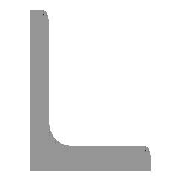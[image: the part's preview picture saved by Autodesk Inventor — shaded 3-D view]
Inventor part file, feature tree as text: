
AUTODESK INVENTOR PART (.ipt)
format: ipt  version: 2013 (Build 170138000, 138)  size: 118,784 bytes
history: native  units: mm (DEFAULTED — no unit token found)
features: other x4, sketch x2, plane x1
ambient origin geometry x8: Origin, YZ Plane, XZ Plane, XY Plane, X Axis, Y Axis, Z Axis, Center Point
bodies: Solid1 (feature_tree), Body (feature_tree)
feature tree (7):
  parser-record x1  (decoder bookkeeping rows leaked as tree rows — omitted from the tree; the rows remain in map.json)
  other  "Driven Length"
  other  "Start plane"
  other  "End plane"
  sketch  "Sketch3"  dims[d0=76.2mm]
  plane  "Work Plane3"
  sketch  "Sketch4"  dims[d1=76.2mm d2=6.35mm d3=6.35mm d4=13016.611mm d5=0.0mm d10=0.0mm d11=0.0mm d12=-0.0mm d13=13016.611mm d14=7.874mm d15=3.81mm d16=90.0deg d17=13016.611mm]
